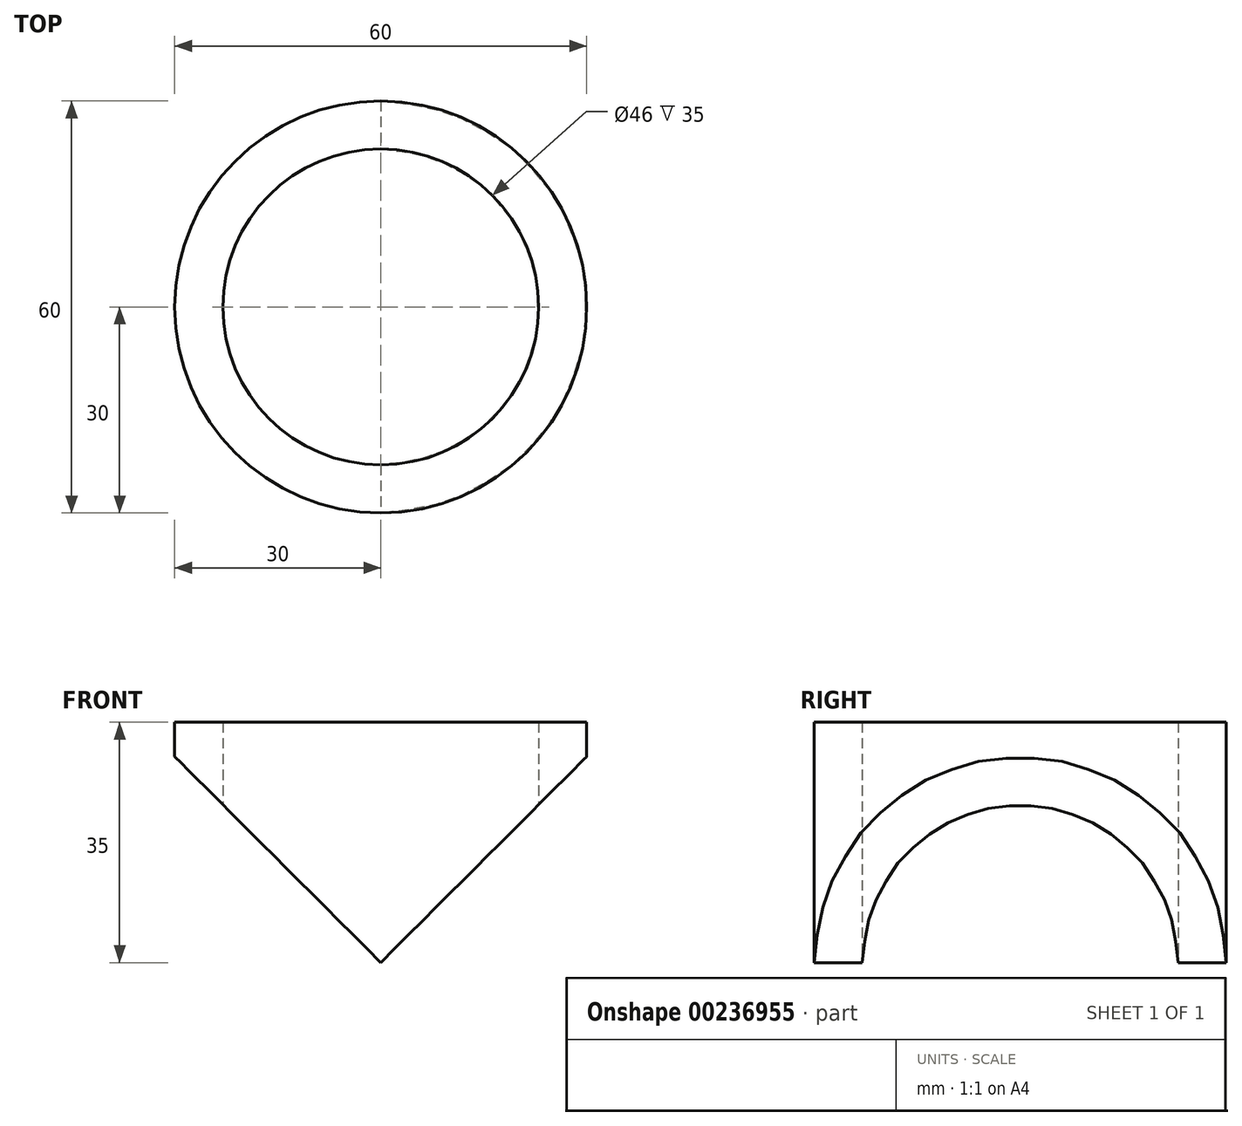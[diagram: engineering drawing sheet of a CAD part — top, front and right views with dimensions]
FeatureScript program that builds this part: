
annotation { "Feature Type Name" : "Feature", "Feature Type Description" : "" }
export const myFeature = defineFeature(function(context is Context, id is Id, definition is map)
    precondition{}
    {
        {
            var Q0;
            Q0=qCreatedBy(makeId("Top.planeOp"),FACE);
            var sketch = newSketch(context, id + "F0", { "sketchPlane" : qUnion([Q0])});
            skCircle(sketch, "E0", {"center": v(0, 0) * mm, "radius": 30 * mm});
            skCircle(sketch, "E1", {"center": v(0, 0) * mm, "radius": 23 * mm});
            skSolve(sketch);
        }
        {
            var Q0;
            Q0 = qSketchRegion(id + "F0", true);
            extrude(context, id + "F1", {"entities" : qUnion([Q0]), "depth" : 35 * mm});
        }
        {
            var Q0;
            Q0=qCreatedBy(makeId("Front.planeOp"),FACE);
            var sketch = newSketch(context, id + "F2", { "sketchPlane" : qUnion([Q0])});
            skLineSegment(sketch, "E2", {"start": v(-30, 0) * mm, "end": v(-30, 35) * mm});
            skLineSegment(sketch, "E3", {"start": v(30, 35) * mm, "end": v(30, 0) * mm});
            skLineSegment(sketch, "E4.0", {"start": v(-30, 0) * mm, "end": v(30, 0) * mm});
            skLineSegment(sketch, "E5.0", {"start": v(-30, 35) * mm, "end": v(30, 35) * mm});
            skLineSegment(sketch, "E6", {"start": v(-30, 30) * mm, "end": v(0, 0) * mm});
            skLineSegment(sketch, "E7", {"start": v(0, 0) * mm, "end": v(30, 30) * mm});
            skSolve(sketch);
        }
        {
            var Q0;
            {var subQ3=sQuery(id+"F2.wireOp",EDGE,"E6");Q0=makeQuery(id+"F2.imprint","IMPRINT",FACE,{"disambiguationData":[TD([[makeQuery(id+"F2.imprint","IMPRINT",EDGE,{"derivedFrom":subQ3}),-1.0]])]});}
            var Q1;
            {var subQ3=sQuery(id+"F2.wireOp",EDGE,"E7");Q1=makeQuery(id+"F2.imprint","IMPRINT",FACE,{"disambiguationData":[TD([[makeQuery(id+"F2.imprint","IMPRINT",EDGE,{"derivedFrom":subQ3}),-1.0]])]});}
            extrude(context, id + "F3", {"entities" : qUnion([Q0, Q1]), "operationType" : NewBodyOperationType.REMOVE, "oppositeDirection" : true, "depth" : 40 * mm, "hasSecondDirection" : true, "secondDirectionOppositeDirection" : false, "secondDirectionDepth" : 40 * mm});
        }
    });
